# Revit family: KS Husky, Typ II-13, Ø108-139,7
name_source: partatom
category: HLS-Bauteile
revit_build: Autodesk Revit 2017 (Build: 20190507_1515(x64)
units: mm (PartAtom-declared; Revit-internal decimal feet)

## family parameters
Arbeitsebenenbasiert = Ja
Beim Laden mit Abzugskörper schneiden = Nein
Bemaßung runder Anschluss = Durchmesser verwenden
Gemeinsam genutzt = Ja
Immer vertikal = Nein
Raumberechnungspunkt = Nein
Teiletyp = Normal

## types (6) — shared parameters
DVS = 6 mm  [stored 0.019685 ft]
Firma = MEFA Befestigungs- und Montagesysteme GmbH
H1 = 2 mm  [stored 0.00656168 ft]
H2 = 4 mm  [stored 0.0131234 ft]
HGA = 22 mm  [stored 0.0721785 ft]
L = 42 mm  [stored 0.137795 ft]
MB = 25 mm  [stored 0.082021 ft]
MD = 3 mm  [stored 0.00984252 ft]
Vorgabe-Ansicht = 1219 mm

## per-type parameters (varying)
- Kälteschelle Husky, Typ II-13, M10/M12, Ø108: A=42 mm  [stored 0.137795 ft]; Anschluss=M10/M12; Anschlußhöhe=42 mm; Artikelnummer=6831081; B=187 mm  [stored 0.613517 ft]; Baustoffklasse=B2; Breite=187 mm  [stored 0.613517 ft]; D=108 mm  [stored 0.354331 ft]; D0=143 mm  [stored 0.46916 ft]; DF1=20 mm  [stored 0.0656168 ft]; DF2=19 mm  [stored 0.062336 ft]; DS=18 mm  [stored 0.0590551 ft]; Dichte Kern=120 kg/m³; Dämmkörper=KA/PU; Dämmstärke=18 mm  [stored 0.0590551 ft]; EAN=4250928440587; Fabrikat=MEFA; Gewicht=0.35 kg; Gewicht pro Bauteil=0.35 kg; H=170 mm  [stored 0.557743 ft]; Kurztext1=Kälteschelle Husky II 13; Kurztext2=108 mm Iso 18 x 42 mm M10/M12; Material=Stahl; Material Mantel=Kunststoff; Materialname=DD11; Mengeneinheit=St; Oberflaeche=galvanisch verzinkt; R=72 mm; RM=74 mm; Rohraußendurchmesser Stahl=108 mm; Rohrschellentyp=Trabant; S=167 mm  [stored 0.5479 ft]; Schalenlänge=42 mm; Typ=II 13; Wasserdampfdiffusionswiderstand=7000 µ; Wärmeleitfähigkeit=0.029 W/mK; max. Temperaturbeständigkeit=105 °C; max. zul. Last=1.01 kN; mittl. Nenndruckfestigkeit Kern=1,35 N/mm²; stat. Belastung Kern=0,27 N/mm²; vpe=8 St
- Kälteschelle Husky, Typ II-13, M10/M12, Ø110: A=42 mm  [stored 0.137795 ft]; Anschluss=M10/M12; Anschlußhöhe=42 mm; Artikelnummer=6831101; B=187 mm  [stored 0.613517 ft]; Baustoffklasse=B2; Breite=187 mm  [stored 0.613517 ft]; D=110 mm  [stored 0.360892 ft]; D0=145 mm  [stored 0.475722 ft]; DF1=19 mm  [stored 0.062336 ft]; DF2=18 mm  [stored 0.0590551 ft]; DS=18 mm  [stored 0.0590551 ft]; Dichte Kern=120 kg/m³; Dämmkörper=KA/PU; Dämmstärke=18 mm  [stored 0.0590551 ft]; EAN=4250928440594; Fabrikat=MEFA; Gewicht=0.35 kg; Gewicht pro Bauteil=0.35 kg; H=172 mm; Kurztext1=Kälteschelle Husky II 13; Kurztext2=110 mm Iso 18 x 42 mm M10/M12; Material=Stahl; Material Mantel=Kunststoff; Materialname=DD11; Mengeneinheit=St; Oberflaeche=galvanisch verzinkt; R=73 mm; RM=75 mm  [stored 0.246063 ft]; Rohraußendurchmesser Kunststoff=110 mm; Rohrschellentyp=Trabant; S=168 mm  [stored 0.551181 ft]; Schalenlänge=42 mm; Typ=II 13; Wasserdampfdiffusionswiderstand=7000 µ; Wärmeleitfähigkeit=0.029 W/mK; max. Temperaturbeständigkeit=105 °C; max. zul. Last=1.02 kN; mittl. Nenndruckfestigkeit Kern=1,35 N/mm²; stat. Belastung Kern=0,27 N/mm²; vpe=4 St
- Kälteschelle Husky, Typ II-13, M10/M12, Ø114,3: A=41 mm; Anschluss=M10/M12; Anschlußhöhe=40 mm; Artikelnummer=6831141; B=192 mm; Baustoffklasse=B2; Breite=192 mm; D=114 mm; D0=147 mm; DF1=20 mm  [stored 0.0656168 ft]; DF2=20 mm  [stored 0.0656168 ft]; DS=16 mm  [stored 0.0524934 ft]; Dichte Kern=120 kg/m³; Dämmkörper=KA/PU; Dämmstärke=16 mm  [stored 0.0524934 ft]; EAN=4250928440600; Fabrikat=MEFA; Gewicht=0.36 kg; Gewicht pro Bauteil=0.36 kg; H=174 mm; Kurztext1=Kälteschelle Husky II 13; Kurztext2=114,3 mm Iso 16 x 42 mm M10/M12; Material=Stahl; Material Mantel=Kunststoff; Materialname=DD11; Mengeneinheit=St; Oberflaeche=galvanisch verzinkt; R=74 mm; RM=76 mm; Rohraußendurchmesser Stahl=114,3 mm; Rohrschellentyp=Trabant; S=172 mm; Schalenlänge=42 mm; Typ=II 13; Wasserdampfdiffusionswiderstand=7000 µ; Wärmeleitfähigkeit=0.029 W/mK; max. Temperaturbeständigkeit=105 °C; max. zul. Last=1.04 kN; mittl. Nenndruckfestigkeit Kern=1,35 N/mm²; stat. Belastung Kern=0,27 N/mm²; vpe=4 St
- Kälteschelle Husky, Typ II-13, M10/M12, Ø125: A=46 mm  [stored 0.150919 ft]; Anschluss=M10/M12; Anschlußhöhe=45 mm; Artikelnummer=6831251; B=215 mm; Baustoffklasse=B2; Breite=215 mm; D=125 mm  [stored 0.410105 ft]; D0=168 mm  [stored 0.551181 ft]; DF1=21 mm  [stored 0.0688976 ft]; DF2=21 mm  [stored 0.0688976 ft]; DS=22 mm  [stored 0.0721785 ft]; Dichte Kern=120 kg/m³; Dämmkörper=KA/PU; Dämmstärke=22 mm  [stored 0.0721785 ft]; EAN=4250928440617; Fabrikat=MEFA; Gewicht=0.41 kg; Gewicht pro Bauteil=0.41 kg; H=195 mm; Kurztext1=Kälteschelle Husky II 13; Kurztext2=125 mm Iso 22 x 42 mm M10/M12; Material=Stahl; Material Mantel=Kunststoff; Materialname=DD11; Mengeneinheit=St; Oberflaeche=galvanisch verzinkt; R=84 mm  [stored 0.275591 ft]; RM=87 mm; Rohraußendurchmesser Kunststoff=125 mm; Rohrschellentyp=Trabant; S=194 mm; Schalenlänge=42 mm; Typ=II 13; Wasserdampfdiffusionswiderstand=7000 µ; Wärmeleitfähigkeit=0.029 W/mK; max. Temperaturbeständigkeit=105 °C; max. zul. Last=1.17 kN; mittl. Nenndruckfestigkeit Kern=1,35 N/mm²; stat. Belastung Kern=0,27 N/mm²; vpe=4 St
- Kälteschelle Husky, Typ II-13, M10/M12, Ø133: A=42 mm  [stored 0.137795 ft]; Artikelnummer=6831331; B=215 mm; Breite=0 mm  [stored 0 ft]; D=133 mm  [stored 0.436352 ft]; D0=168 mm  [stored 0.551181 ft]; DF1=21 mm  [stored 0.0688976 ft]; DF2=21 mm  [stored 0.0688976 ft]; DS=18 mm  [stored 0.0590551 ft]; Dämmstärke=0 mm  [stored 0 ft]; Gewicht=0.00 kg; Gewicht pro Bauteil=0.00 kg; H=195 mm; R=84 mm  [stored 0.275591 ft]; RM=87 mm; S=194 mm; max. zul. Last=0.00 kN
- Kälteschelle Husky, Typ II-13, M10/M12, Ø139,7: A=42 mm  [stored 0.137795 ft]; Anschluss=M10/M12; Anschlußhöhe=42 mm; Artikelnummer=6831401; B=220 mm; Baustoffklasse=B2; Breite=220 mm; D=140 mm; D0=175 mm; DF1=20 mm  [stored 0.0656168 ft]; DF2=20 mm  [stored 0.0656168 ft]; DS=18 mm  [stored 0.0590551 ft]; Dichte Kern=120 kg/m³; Dämmkörper=KA/PU; Dämmstärke=18 mm  [stored 0.0590551 ft]; EAN=4250928440631; Fabrikat=MEFA; Gewicht=0.41 kg; Gewicht pro Bauteil=0.41 kg; H=202 mm; Kurztext1=Kälteschelle Husky II 13; Kurztext2=139,7 mm Iso 18 x 42 mm M10/M12; Material=Stahl; Material Mantel=Kunststoff; Materialname=DD11; Mengeneinheit=St; Oberflaeche=galvanisch verzinkt; R=88 mm; RM=90 mm; Rohraußendurchmesser Stahl=139,7 mm; Rohrschellentyp=Trabant; S=200 mm; Schalenlänge=42 mm; Typ=II 13; Wasserdampfdiffusionswiderstand=7000 µ; Wärmeleitfähigkeit=0.029 W/mK; max. Temperaturbeständigkeit=105 °C; max. zul. Last=1.24 kN; mittl. Nenndruckfestigkeit Kern=1,35 N/mm²; stat. Belastung Kern=0,27 N/mm²; vpe=4 St

note: [stored X ft] marks values corroborated as IEEE doubles in the binary element streams (Revit-internal decimal feet)

## geometry (parser evidence)
native form markers: Sweep x3
no freeform markers — native parametric forms only
